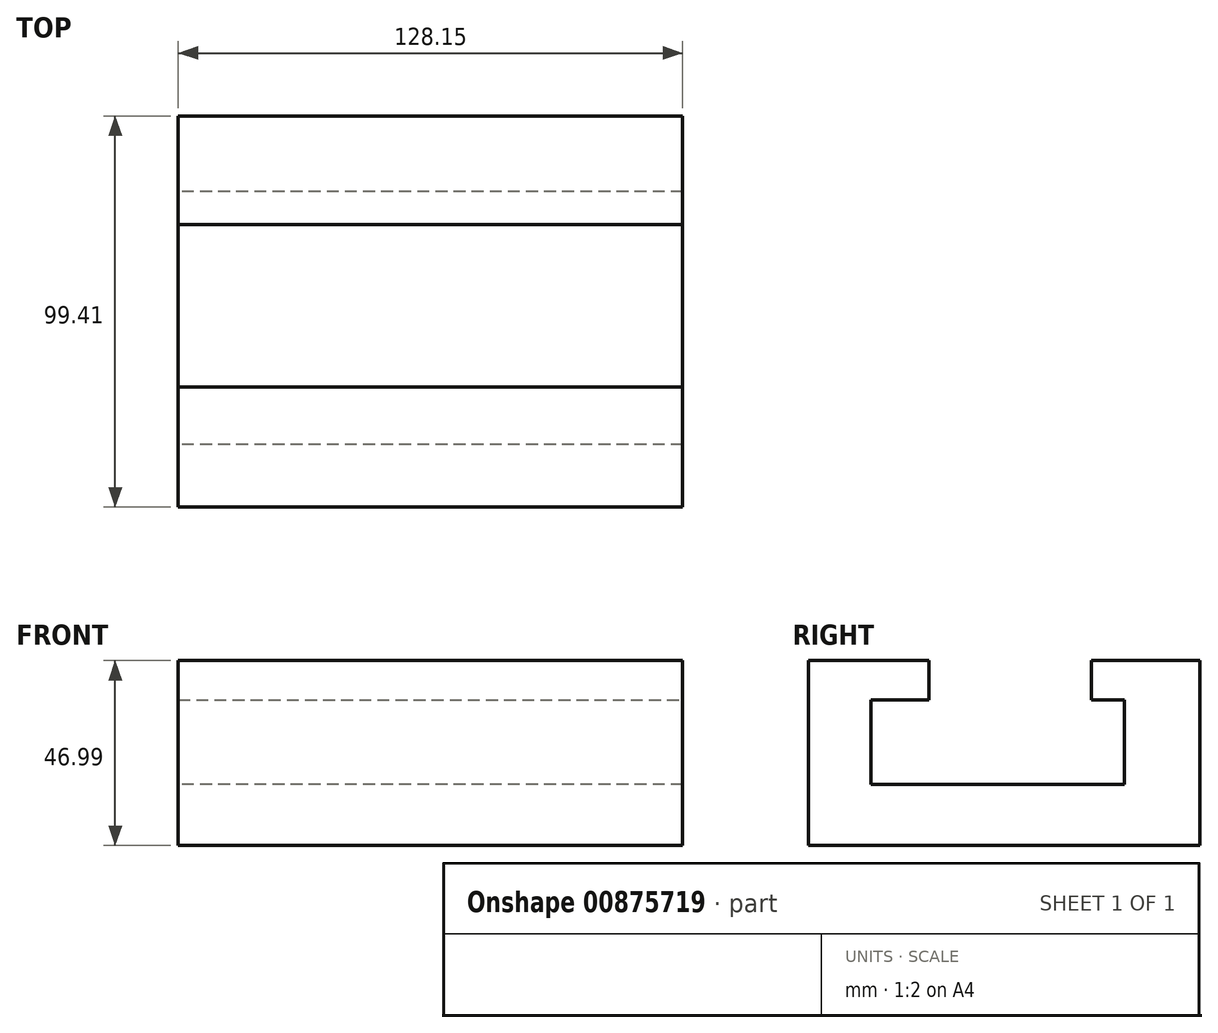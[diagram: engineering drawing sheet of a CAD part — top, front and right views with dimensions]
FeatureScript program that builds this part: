
annotation { "Feature Type Name" : "Feature", "Feature Type Description" : "" }
export const myFeature = defineFeature(function(context is Context, id is Id, definition is map)
    precondition{}
    {
        {
            var Q0;
            Q0=qCreatedBy(makeId("Top.planeOp"),FACE);
            var sketch = newSketch(context, id + "F0", { "sketchPlane" : qUnion([Q0])});
            skLineSegment(sketch, "E0.bottom", {"start": v(-49.02, -42.9) * mm, "end": v(79.13, -42.9) * mm});
            skLineSegment(sketch, "E0.top", {"start": v(-49.02, 56.51) * mm, "end": v(79.13, 56.51) * mm});
            skLineSegment(sketch, "E0.left", {"start": v(-49.02, -42.9) * mm, "end": v(-49.02, 56.51) * mm});
            skLineSegment(sketch, "E0.right", {"start": v(79.13, -42.9) * mm, "end": v(79.13, 56.51) * mm});
            skSolve(sketch);
        }
        {
            var Q0;
            Q0=makeQuery(id+"F0.imprint","IMPRINT",FACE,{"disambiguationData":[TD([[makeQuery(id+"F0.imprint","IMPRINT",EDGE,{"derivedFrom":sQuery(id+"F0.wireOp",EDGE,"E0.bottom")}),1.0]])]});
            extrude(context, id + "F1", {"entities" : qUnion([Q0]), "depth" : 47 * mm, "offsetDistance" : 25.4 * mm});
        }
        {
            var Q0;
            Q0=makeQuery(id+"F1.opExtrude","SWEPT_FACE",FACE,{"disambiguationData":[OSD([sQuery(id+"F0.wireOp",EDGE,"E0.left")])]});
            cPlane(context, id + "F2", {"entities" : qUnion([Q0]), "cplaneType" : CPlaneType.OFFSET, "offset" : 25.4 * mm, "oppositeDirection" : true, "width" : 152.4 * mm, "height" : 152.4 * mm});
        }
        {
            var Q0;
            Q0=qCreatedBy(id+"F2.planeOp",FACE);
            var sketch = newSketch(context, id + "F3", { "sketchPlane" : qUnion([Q0])});
            skLineSegment(sketch, "E1.bottom", {"start": v(-37.32, 37.03) * mm, "end": v(27.04, 37.03) * mm});
            skLineSegment(sketch, "E1.top", {"start": v(-37.32, 15.51) * mm, "end": v(27.04, 15.51) * mm});
            skLineSegment(sketch, "E1.left", {"start": v(-37.32, 37.03) * mm, "end": v(-37.32, 15.51) * mm});
            skLineSegment(sketch, "E1.right", {"start": v(27.04, 37.03) * mm, "end": v(27.04, 15.51) * mm});
            skSolve(sketch);
        }
        {
            var Q0;
            Q0 = qSketchRegion(id + "F3", true);
            extrude(context, id + "F4", {"entities" : qUnion([Q0]), "operationType" : NewBodyOperationType.REMOVE, "endBound" : BoundingType.THROUGH_ALL, "oppositeDirection" : true, "depth" : 136.4 * mm, "offsetDistance" : 25.4 * mm});
        }
        {
            var Q0;
            Q0=qCreatedBy(id+"F2.planeOp",FACE);
            var sketch = newSketch(context, id + "F5", { "sketchPlane" : qUnion([Q0])});
            skLineSegment(sketch, "E2.bottom", {"start": v(-28.96, 56.43) * mm, "end": v(12.34, 56.43) * mm});
            skLineSegment(sketch, "E2.top", {"start": v(-28.96, 33.19) * mm, "end": v(12.34, 33.19) * mm});
            skLineSegment(sketch, "E2.left", {"start": v(-28.96, 56.43) * mm, "end": v(-28.96, 33.19) * mm});
            skLineSegment(sketch, "E2.right", {"start": v(12.34, 56.43) * mm, "end": v(12.34, 33.19) * mm});
            skSolve(sketch);
        }
        {
            var Q0;
            Q0 = qSketchRegion(id + "F5", true);
            extrude(context, id + "F6", {"entities" : qUnion([Q0]), "operationType" : NewBodyOperationType.REMOVE, "oppositeDirection" : true, "depth" : 167.9 * mm, "offsetDistance" : 25.4 * mm});
        }
        {
            var Q0;
            Q0 = qSketchRegion(id + "F3", true);
            extrude(context, id + "F7", {"entities" : qUnion([Q0]), "operationType" : NewBodyOperationType.REMOVE, "depth" : 64 * mm, "offsetDistance" : 25.4 * mm});
        }
        {
            var Q0;
            Q0=makeQuery(id+"F5.imprint","IMPRINT",FACE,{"disambiguationData":[TD([[makeQuery(id+"F5.imprint","IMPRINT",EDGE,{"derivedFrom":sQuery(id+"F5.wireOp",EDGE,"E2.bottom")}),-1.0]])]});
            extrude(context, id + "F8", {"entities" : qUnion([Q0]), "operationType" : NewBodyOperationType.REMOVE, "depth" : 88.14 * mm, "offsetDistance" : 25.4 * mm});
        }
    });
